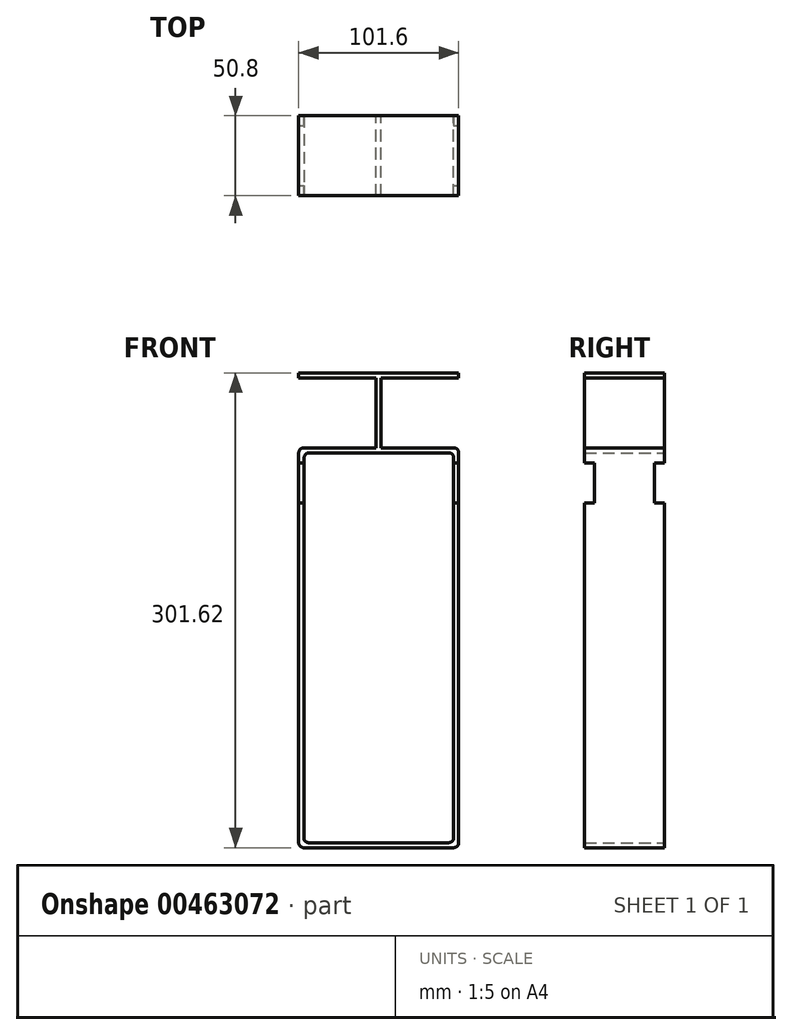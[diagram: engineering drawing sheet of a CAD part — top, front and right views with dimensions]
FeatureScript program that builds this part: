
annotation { "Feature Type Name" : "Feature", "Feature Type Description" : "" }
export const myFeature = defineFeature(function(context is Context, id is Id, definition is map)
    precondition{}
    {
        {
            var Q0;
            Q0=qCreatedBy(makeId("Front.planeOp"),FACE);
            var sketch = newSketch(context, id + "F0", { "sketchPlane" : qUnion([Q0])});
            skLineSegment(sketch, "E0", {"start": v(-56.92, 210.14) * mm, "end": v(-7.7, 210.14) * mm});
            skLineSegment(sketch, "E1", {"start": v(44.68, 210.14) * mm, "end": v(44.68, -43.86) * mm});
            skLineSegment(sketch, "E2", {"start": v(44.68, -43.86) * mm, "end": v(-56.92, -43.86) * mm});
            skLineSegment(sketch, "E3", {"start": v(-56.92, -43.86) * mm, "end": v(-56.92, 210.14) * mm});
            skLineSegment(sketch, "E4", {"start": v(-53.5, 206.96) * mm, "end": v(41.5, 206.96) * mm});
            skLineSegment(sketch, "E5", {"start": v(41.5, 206.96) * mm, "end": v(41.5, -40.69) * mm});
            skLineSegment(sketch, "E6", {"start": v(41.5, -40.69) * mm, "end": v(-53.75, -40.69) * mm});
            skLineSegment(sketch, "E7", {"start": v(-53.75, -40.69) * mm, "end": v(-53.5, 206.96) * mm});
            skLineSegment(sketch, "E8", {"start": v(-7.7, 210.14) * mm, "end": v(-7.7, 254.59) * mm});
            skLineSegment(sketch, "E9", {"start": v(-7.7, 254.59) * mm, "end": v(-56.92, 254.59) * mm});
            skLineSegment(sketch, "E10", {"start": v(-56.92, 254.59) * mm, "end": v(-56.92, 257.76) * mm});
            skLineSegment(sketch, "E11", {"start": v(-56.92, 257.76) * mm, "end": v(44.68, 257.76) * mm});
            skLineSegment(sketch, "E12", {"start": v(44.68, 254.59) * mm, "end": v(-4.53, 254.59) * mm});
            skLineSegment(sketch, "E13", {"start": v(-4.53, 254.59) * mm, "end": v(-4.53, 210.14) * mm});
            skLineSegment(sketch, "E14", {"start": v(44.68, 254.59) * mm, "end": v(44.68, 257.76) * mm});
            skLineSegment(sketch, "E15.trimOffspring", {"start": v(-4.53, 210.14) * mm, "end": v(44.68, 210.14) * mm});
            skSolve(sketch);
        }
        {
            var Q0;
            Q0=makeQuery(id+"F0.imprint","IMPRINT",FACE,{"disambiguationData":[TD([[makeQuery(id+"F0.imprint","IMPRINT",EDGE,{"derivedFrom":sQuery(id+"F0.wireOp",EDGE,"E0")}),-1.0]])]});
            extrude(context, id + "F1", {"entities" : qUnion([Q0]), "depth" : 50.8 * mm});
        }
        {
            var Q0;
            Q0=makeQuery(id+"F1.opExtrude","SWEPT_EDGE",EDGE,{"disambiguationData":[OSD([sQuery(id+"F0.wireOp",EDGE,"E0"),sQuery(id+"F0.wireOp",EDGE,"E3")])]});
            var Q1;
            Q1=makeQuery(id+"F1.opExtrude","SWEPT_EDGE",EDGE,{"disambiguationData":[OSD([sQuery(id+"F0.wireOp",EDGE,"E4"),sQuery(id+"F0.wireOp",EDGE,"E7")])]});
            var Q2;
            Q2=makeQuery(id+"F1.opExtrude","SWEPT_EDGE",EDGE,{"disambiguationData":[OSD([sQuery(id+"F0.wireOp",EDGE,"E1"),sQuery(id+"F0.wireOp",EDGE,"E15.trimOffspring")])]});
            var Q3;
            Q3=makeQuery(id+"F1.opExtrude","SWEPT_EDGE",EDGE,{"disambiguationData":[OSD([sQuery(id+"F0.wireOp",EDGE,"E4"),sQuery(id+"F0.wireOp",EDGE,"E5")])]});
            var Q4;
            Q4=makeQuery(id+"F1.opExtrude","SWEPT_EDGE",EDGE,{"disambiguationData":[OSD([sQuery(id+"F0.wireOp",EDGE,"E1"),sQuery(id+"F0.wireOp",EDGE,"E2")])]});
            var Q5;
            Q5=makeQuery(id+"F1.opExtrude","SWEPT_EDGE",EDGE,{"disambiguationData":[OSD([sQuery(id+"F0.wireOp",EDGE,"E5"),sQuery(id+"F0.wireOp",EDGE,"E6")])]});
            var Q6;
            Q6=makeQuery(id+"F1.opExtrude","SWEPT_EDGE",EDGE,{"disambiguationData":[OSD([sQuery(id+"F0.wireOp",EDGE,"E2"),sQuery(id+"F0.wireOp",EDGE,"E3")])]});
            var Q7;
            Q7=makeQuery(id+"F1.opExtrude","SWEPT_EDGE",EDGE,{"disambiguationData":[OSD([sQuery(id+"F0.wireOp",EDGE,"E6"),sQuery(id+"F0.wireOp",EDGE,"E7")])]});
            fillet(context, id + "F2", {"entities" : qUnion([Q0, Q1, Q2, Q3, Q4, Q5, Q6, Q7]), "radius" : 3.17 * mm, "tangentPropagation" : true, "allowEdgeOverflow" : false});
        }
        {
            var Q0;
            Q0=makeQuery(id+"F1.opExtrude","SWEPT_FACE",FACE,{"disambiguationData":[OSD([sQuery(id+"F0.wireOp",EDGE,"E1")])]});
            var sketch = newSketch(context, id + "F3", { "sketchPlane" : qUnion([Q0])});
            skLineSegment(sketch, "E16", {"start": v(-69.85, 200.61) * mm, "end": v(-44.45, 200.61) * mm});
            skLineSegment(sketch, "E17", {"start": v(-44.45, 200.61) * mm, "end": v(-44.45, 175.21) * mm});
            skLineSegment(sketch, "E18", {"start": v(-44.45, 175.21) * mm, "end": v(-69.85, 175.21) * mm});
            skLineSegment(sketch, "E19", {"start": v(-69.85, 175.21) * mm, "end": v(-69.85, 200.61) * mm});
            skLineSegment(sketch, "E20", {"start": v(-6.35, 200.61) * mm, "end": v(-6.35, 175.21) * mm});
            skLineSegment(sketch, "E21", {"start": v(-6.35, 175.21) * mm, "end": v(8.39, 175.21) * mm});
            skLineSegment(sketch, "E22", {"start": v(8.39, 175.21) * mm, "end": v(8.39, 200.61) * mm});
            skLineSegment(sketch, "E23", {"start": v(8.39, 200.61) * mm, "end": v(-6.35, 200.61) * mm});
            skSolve(sketch);
        }
        {
            var Q0;
            {var subQ0=sQuery(id+"F3.wireOp",EDGE,"E19");Q0=makeQuery(id+"F3.imprint","IMPRINT",FACE,{"disambiguationData":[TD([[makeQuery(id+"F3.imprint","IMPRINT",EDGE,{"derivedFrom":subQ0}),-1.0]])]});}
            var Q1;
            {var subQ0=sQuery(id+"F3.wireOp",EDGE,"E17");Q1=makeQuery(id+"F3.imprint","IMPRINT",FACE,{"disambiguationData":[TD([[makeQuery(id+"F3.imprint","IMPRINT",EDGE,{"derivedFrom":subQ0}),-1.0]])]});}
            var Q2;
            {var subQ0=sQuery(id+"F3.wireOp",EDGE,"E20");Q2=makeQuery(id+"F3.imprint","IMPRINT",FACE,{"disambiguationData":[TD([[makeQuery(id+"F3.imprint","IMPRINT",EDGE,{"derivedFrom":subQ0}),1.0]])]});}
            extrude(context, id + "F4", {"entities" : qUnion([Q0, Q1, Q2]), "operationType" : NewBodyOperationType.REMOVE, "oppositeDirection" : true, "depth" : 127 * mm});
        }
    });
